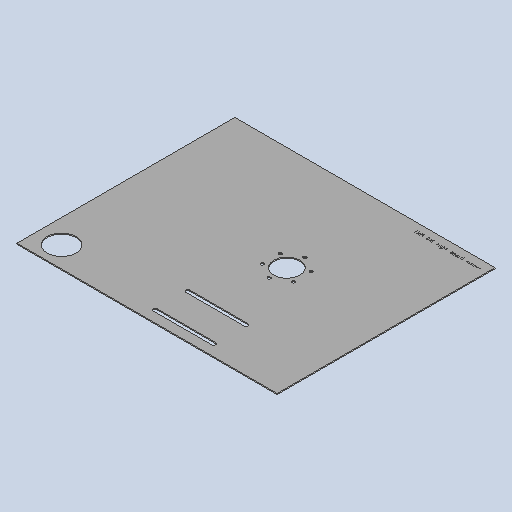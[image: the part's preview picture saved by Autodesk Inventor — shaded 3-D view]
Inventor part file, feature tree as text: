
AUTODESK INVENTOR PART (.ipt)
format: ipt  version: 2025 (Build 290162010, 162A)  size: 342,528 bytes
history: native  units: mm
features: other x6, sketch x5, extrude x2, sheet_metal_op x1, pattern_circular x1
ambient origin geometry x8: Origin, YZ Plane, XZ Plane, XY Plane, X Axis, Y Axis, Z Axis, Center Point
bodies: Solid1 (feature_tree)
feature tree (15):
  other  "TRM 016 right board main++"
  sheet_metal_op  "Face1"
  pattern_circular  "Circular Pattern1"  Count=8  [1 undecoded]
  other  "Mark2"
  other  "A-Side Definition"
  extrude  "Extrusion1"  Depth=320.0mm
  extrude  "Extrusion2"  Depth=10.0mm
  sketch  "Sketch1"  dims[d2=3.0mm d14=80.0mm]
  other  "Plate1"
  sketch  "Sketch3"  dims[d15=320.0mm d17=320.0mm]
  sketch  "Sketch4"  dims[d19=10.0mm d20=55.0mm]
  sketch  "Sketch5"  dims[d21=3.0mm]
  sketch  "Sketch6"  dims[d22=0.0mm d23=60.0mm d24=360.0deg d26=800.0mm d27=670.0mm d28=200.0mm d29=20.0mm d30=20.0mm d31=20.0mm d32=72.8mm d33=89.0mm d34=64.5mm d35=0.0mm d36=0.0mm d37=180.0mm d38=12.0mm d41=100.0mm d42=85.0mm d43=228.0mm d45=5.0mm d46=140.0mm d47=76.0mm d48=76.0mm d49=0.0mm d50=0.0mm]
  other  "Cut1"
  other  "Definition1"
note: 1 required parameter value undecoded (feature->parameter linkage not recoverable at this tier; creation-order binding heuristic only, values carry confidence <= 0.55)
